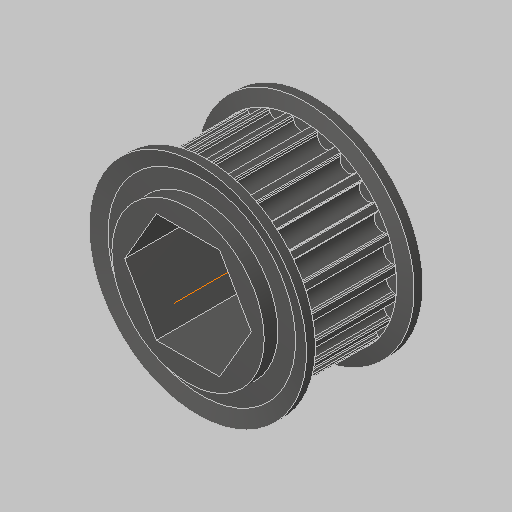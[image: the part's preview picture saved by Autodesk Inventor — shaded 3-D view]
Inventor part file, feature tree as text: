
AUTODESK INVENTOR PART (.ipt)
format: ipt  version: 2023.5 (Build 275446000, 446)  size: 316,416 bytes
history: native  units: in
note: dims shown in document units (in); Inventor stores cm internally (conversion verified against a paired STEP export)
features: other x1, plane x1, mirror x1
ambient origin geometry x8: Origin, YZ Plane, XZ Plane, XY Plane, X Axis, Y Axis, Z Axis, Center Point
bodies: Solid1 (feature_tree)
feature tree (3):
  other  "Work Axis1"
  plane  "Work Plane1"
  mirror  "Mirror1"
